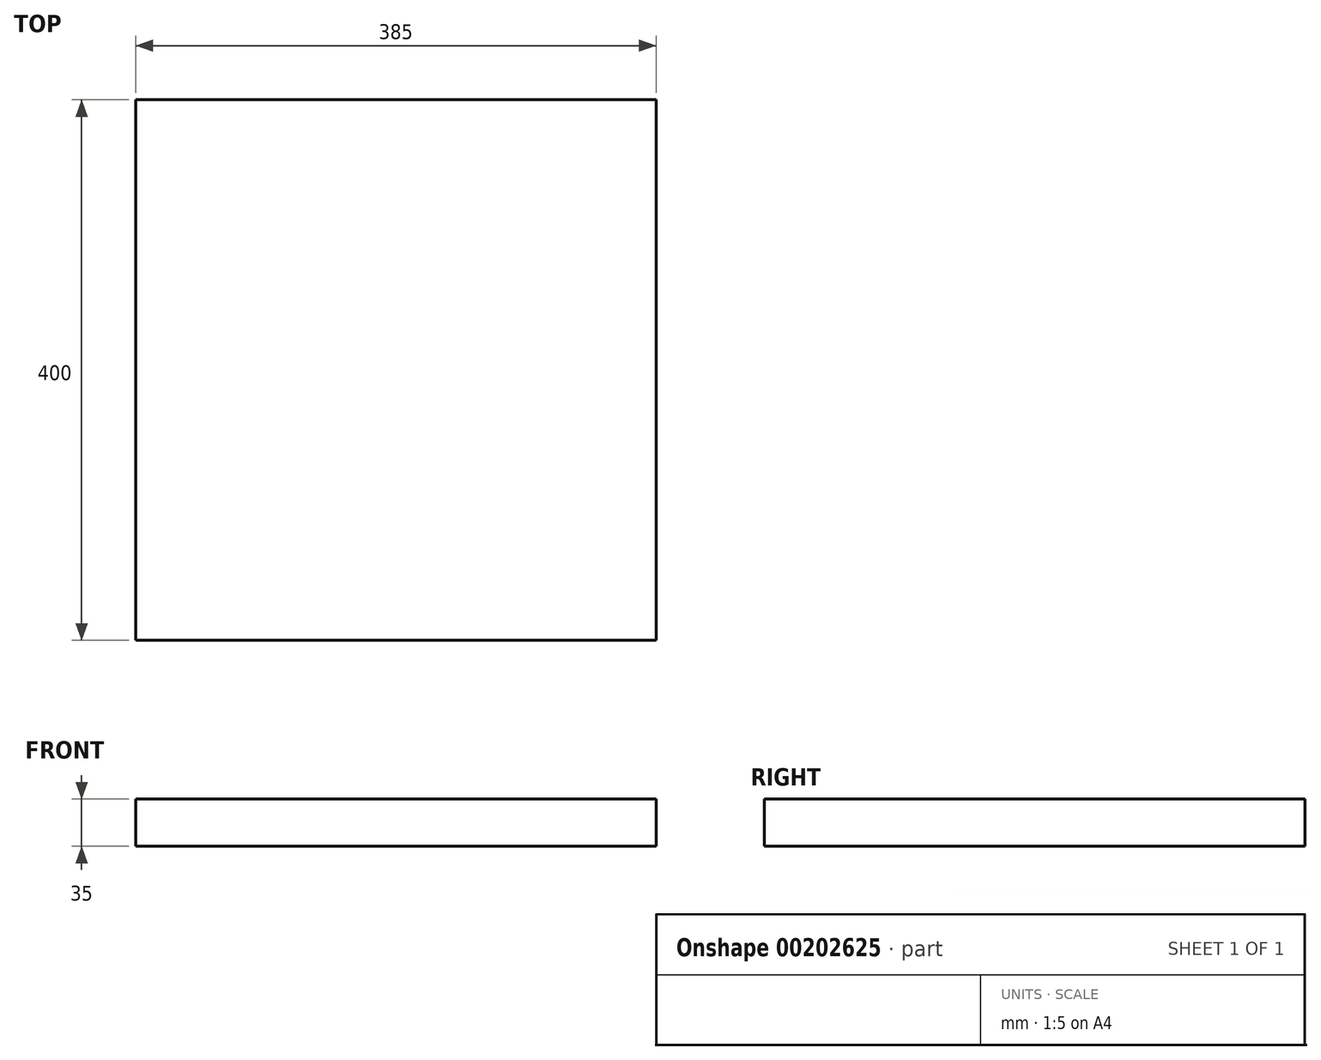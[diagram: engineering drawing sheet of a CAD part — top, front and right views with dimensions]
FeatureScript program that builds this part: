
annotation { "Feature Type Name" : "Feature", "Feature Type Description" : "" }
export const myFeature = defineFeature(function(context is Context, id is Id, definition is map)
    precondition{}
    {
        {
            var Q0;
            Q0=qCreatedBy(makeId("Top.planeOp"),FACE);
            var sketch = newSketch(context, id + "F0", { "sketchPlane" : qUnion([Q0])});
            skLineSegment(sketch, "E0.bottom", {"start": v(-864.34, -235.28) * mm, "end": v(-479.34, -235.28) * mm});
            skLineSegment(sketch, "E0.top", {"start": v(-864.34, 164.72) * mm, "end": v(-479.34, 164.72) * mm});
            skLineSegment(sketch, "E0.left", {"start": v(-864.34, -235.28) * mm, "end": v(-864.34, 164.72) * mm});
            skLineSegment(sketch, "E0.right", {"start": v(-479.34, -235.28) * mm, "end": v(-479.34, 164.72) * mm});
            skSolve(sketch);
        }
        {
            var Q0;
            Q0=makeQuery(id+"F0.imprint","IMPRINT",FACE,{"disambiguationData":[TD([[makeQuery(id+"F0.imprint","IMPRINT",EDGE,{"derivedFrom":sQuery(id+"F0.wireOp",EDGE,"E0.bottom")}),1.0]])]});
            extrude(context, id + "F1", {"entities" : qUnion([Q0]), "depth" : 35 * mm});
        }
    });
